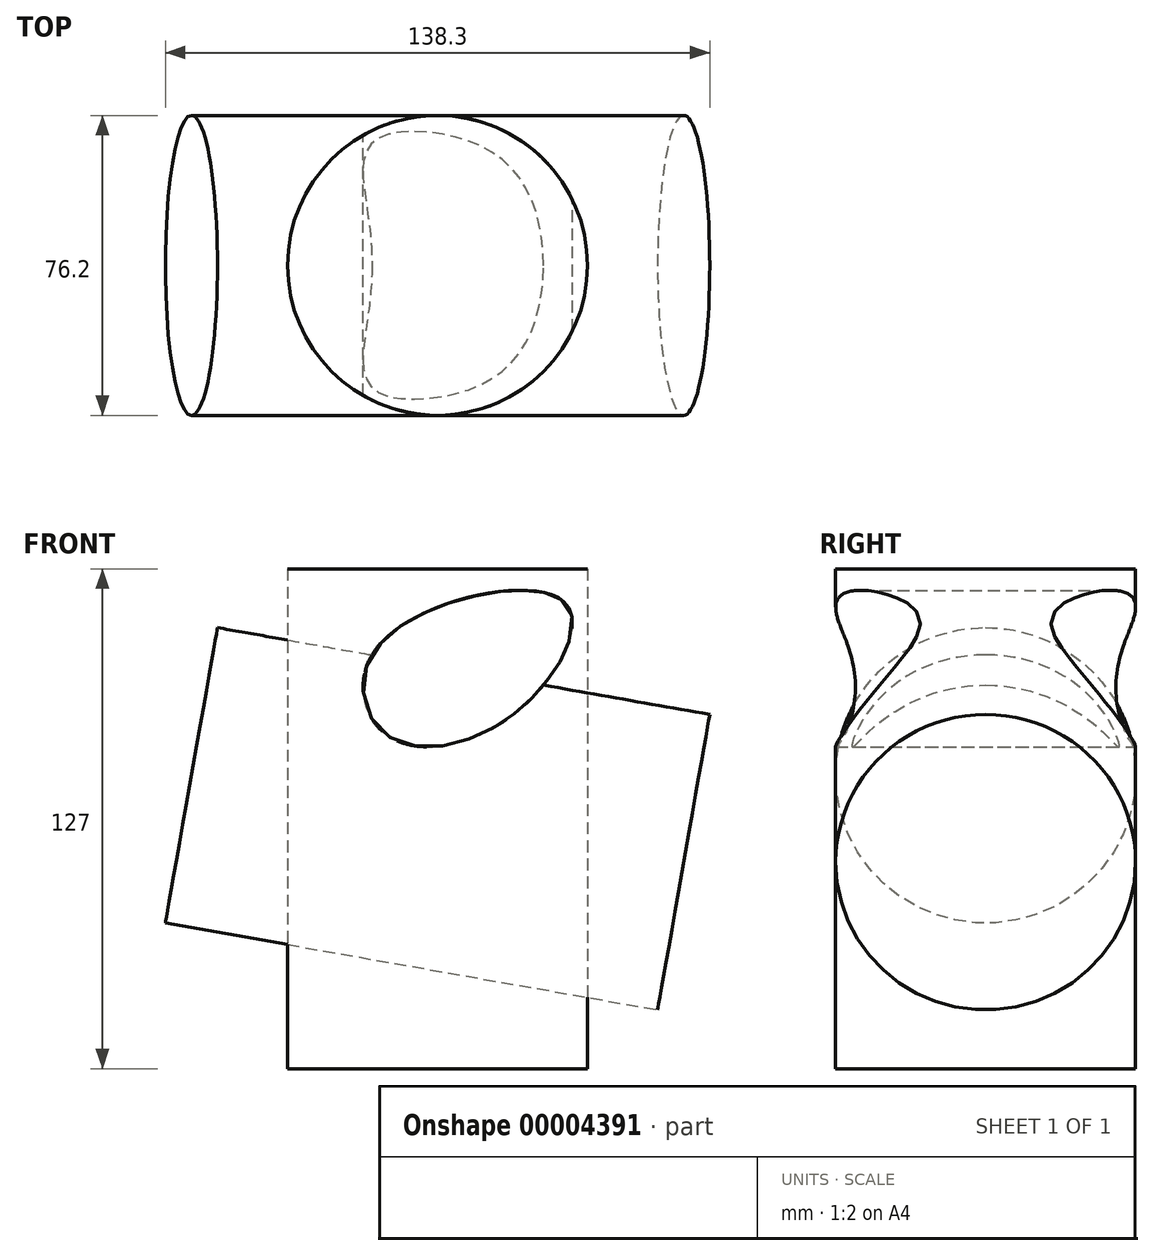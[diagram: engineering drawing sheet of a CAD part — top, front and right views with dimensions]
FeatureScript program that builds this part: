
annotation { "Feature Type Name" : "Feature", "Feature Type Description" : "" }
export const myFeature = defineFeature(function(context is Context, id is Id, definition is map)
    precondition{}
    {
        {
            var Q0;
            Q0=qCreatedBy(makeId("Top.planeOp"),FACE);
            var sketch = newSketch(context, id + "F0", { "sketchPlane" : qUnion([Q0])});
            skCircle(sketch, "E0", {"center": v(0, 0) * mm, "radius": 38.1 * mm});
            skSolve(sketch);
        }
        {
            var Q0;
            Q0=makeQuery(id+"F0.imprint","IMPRINT",FACE,{"disambiguationData":[TD([[makeQuery(id+"F0.imprint","IMPRINT",EDGE,{"derivedFrom":sQuery(id+"F0.wireOp",EDGE,"E0")}),1.0]])]});
            extrude(context, id + "F1", {"entities" : qUnion([Q0]), "endBound" : BoundingType.SYMMETRIC, "depth" : 127 * mm});
        }
        {
            var Q0;
            Q0=qCreatedBy(makeId("Right.planeOp"),FACE);
            var sketch = newSketch(context, id + "F2", { "sketchPlane" : qUnion([Q0])});
            skLineSegment(sketch, "E1", {"start": v(0, 0) * mm, "end": v(-138.33, 0) * mm});
            skSolve(sketch);
        }
        {
            var Q0;
            Q0=makeQuery(id+"F1.opExtrude","SWEPT_BODY",BODY,{"disambiguationData":[OSD([sQuery(id+"F0.wireOp",EDGE,"E0")])]});
            var Q1;
            Q1=sQuery(id+"F2.wireOp",EDGE,"E1");
            transform(context, id + "F3", {"entities" : qUnion([Q0]), "transformType" : TransformType.ROTATION, "transformAxis" : qUnion([Q1]), "angle" : 80 * degree, "makeCopy" : true});
        }
        {
            var Q0;
            Q0=qCreatedBy(makeId("Front.planeOp"),FACE);
            var sketch = newSketch(context, id + "F4", { "sketchPlane" : qUnion([Q0])});
            skFitSpline(sketch, "E2", {"points": [v(-14.51, 44.56) * mm, v(32.23, 55.04) * mm, v(19.62, 26.79) * mm, v(-12.97, 21.33) * mm, v(-14.51, 44.56) * mm]});
            skSolve(sketch);
        }
        {
            var Q0;
            Q0=makeQuery(id+"F4.imprint","IMPRINT",FACE,{"disambiguationData":[TD([[makeQuery(id+"F4.imprint","IMPRINT",EDGE,{"derivedFrom":sQuery(id+"F4.wireOp",EDGE,"E2")}),-1.0]])]});
            extrude(context, id + "F5", {"entities" : qUnion([Q0]), "operationType" : NewBodyOperationType.REMOVE, "endBound" : BoundingType.SYMMETRIC, "oppositeDirection" : true, "depth" : 153.5 * mm});
        }
    });
